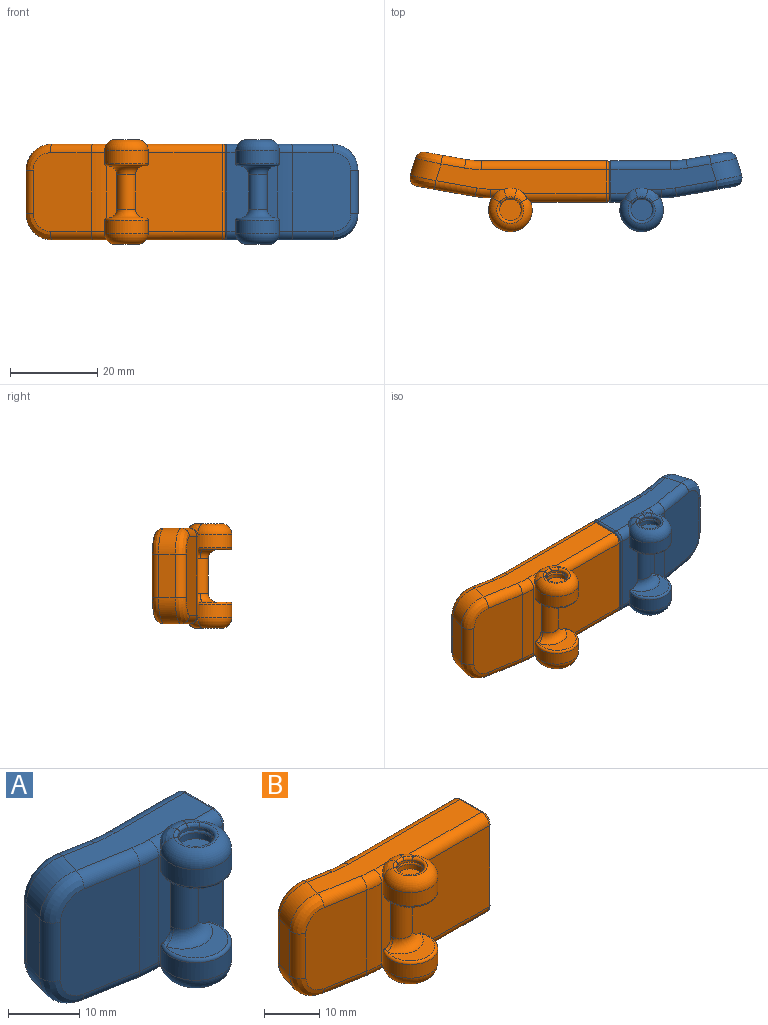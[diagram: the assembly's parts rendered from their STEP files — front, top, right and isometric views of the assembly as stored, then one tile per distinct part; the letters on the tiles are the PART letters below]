
ASSEMBLY  parts=2 mates=1
PART A: 91 faces, bbox 31x19.4x24.6 mm
  f0: plane 24.55x7.21mm, normal (0,0,-1), area 106.2mm2, adj f10,f23,f24,f25,f32,f33,f34,f42
  f1: plane 21x8.5mm, normal (1,0,0), area 116.5mm2, adj f18,f19,f20,f21,f67,f68,f69,f70
  f2: plane 10x3.86mm, normal (-0.96,0.28,0), area 40.3mm2, adj f7,f10,f27,f36
  f3: plane 9x6.24mm, normal (0,0,1), area 26.5mm2, adj f43,f78
  f4: cylinder r=2.25mm len=8.16mm, axis (0,0,1), area 50mm2, adj f13,f17,f77,f78,f80,f81
  f5: plane 9x6.24mm, normal (0,0,-1), area 26.5mm2, adj f44,f81
  f6: cylinder r=5mm len=10mm, axis (0,0,1), area 61.4mm2, adj f13,f17,f40,f41,f44,f60
  f7: cylinder r=6mm len=7.02mm, axis (0.28,0.96,0), area 37.9mm2, adj f2,f15,f28,f37
  f8: cylinder r=20mm len=18mm, axis (0,0,1), area 62.8mm2, adj f9,f16,f24,f30
  f9: plane 18x9.36mm, normal (0.17,0.98,0), area 164.2mm2, adj f8,f25,f26,f27,f28,f29
  f10: cylinder r=6mm len=7.02mm, axis (-0.28,-0.96,0), area 37.9mm2, adj f0,f2,f26,f35
  f11: plane 18x13.34mm, normal (-0.17,-0.98,0), area 236.8mm2, adj f12,f34,f35,f36,f37,f38
  f12: cylinder r=20mm len=18mm, axis (0,0,-1), area 62.8mm2, adj f11,f13,f33,f39
  f13: plane 18.17x2.48mm, normal (0,-1,0), area 28.9mm2, adj f4,f6,f12,f14,f32,f40,f43,f44
  f14: cylinder r=5mm len=10mm, axis (0,0,-1), area 61.4mm2, adj f13,f17,f32,f42,f43,f56
  f15: plane 24.55x7.21mm, normal (0,0,1), area 106.2mm2, adj f7,f29,f30,f31,f38,f39,f40,f41
  f16: plane 18x13.77mm, normal (0,1,0), area 222.6mm2, adj f8,f23,f31,f67,f75,f76
  f17: plane 18.11x5.11mm, normal (0,-1,0), area 72.7mm2, adj f4,f6,f14,f41,f42,f43,f44,f74
  f18: plane 20x4.9mm, normal (0,0,-1), area 98mm2, adj f1,f19,f21,f22
  f19: plane 20x12.25mm, normal (0,1,0), area 245mm2, adj f1,f18,f20,f22
  f20: plane 20x4.9mm, normal (0,0,1), area 98mm2, adj f1,f19,f21,f22
  f21: plane 20x12.25mm, normal (0,-1,0), area 245mm2, adj f1,f18,f20,f22
  f22: plane 12.25x4.9mm, normal (1,0,0), area 60mm2, adj f18,f19,f20,f21
  f23: cylinder r=2mm len=13.77mm, axis (-1,0,0), area 43.2mm2, adj f0,f16,f24,f69
  f24: torus R=22mm, axis (0,0,1), area 11.4mm2, adj f0,f8,f23,f25
  f25: cylinder r=2mm len=5.75mm, axis (-0.98,0.17,0), area 17.2mm2, adj f0,f9,f24,f26
  f26: bspline ~7.26x6.01mm, area 24.7mm2, adj f9,f10,f25,f27
  f27: cylinder r=2mm len=10mm, axis (0,0,-1), area 29.2mm2, adj f2,f9,f26,f28
  f28: bspline ~7.26x7.05mm, area 24.7mm2, adj f7,f9,f27,f29
  f29: cylinder r=2mm len=5.75mm, axis (0.98,-0.17,0), area 17.2mm2, adj f9,f15,f28,f30
  f30: torus R=22mm, axis (0,0,1), area 11.4mm2, adj f8,f15,f29,f31
  f31: cylinder r=2mm len=13.77mm, axis (1,0,0), area 43.2mm2, adj f15,f16,f30,f68
  f32: cylinder r=2mm len=3.06mm, axis (-1,0,0), area 3.5mm2, adj f0,f13,f14,f33,f58
  f33: torus R=18mm, axis (0,0,1), area 10.6mm2, adj f0,f12,f32,f34
  f34: cylinder r=2mm len=9.72mm, axis (0.98,-0.17,0), area 29.9mm2, adj f0,f11,f33,f35
  f35: bspline ~6x5.96mm, area 27.4mm2, adj f10,f11,f34,f36
  f36: cylinder r=2mm len=10mm, axis (0,0,1), area 33.7mm2, adj f2,f11,f35,f37
  f37: bspline ~6x5.96mm, area 27.4mm2, adj f7,f11,f36,f38
  f38: cylinder r=2mm len=9.72mm, axis (-0.98,0.17,0), area 29.9mm2, adj f11,f15,f37,f39
  f39: torus R=18mm, axis (0,0,1), area 10.6mm2, adj f12,f15,f38,f40
  f40: cylinder r=2mm len=3.06mm, axis (1,0,0), area 3.5mm2, adj f6,f13,f15,f39,f59
  f41: cylinder r=2mm len=4mm, axis (-1,0,0), area 9.5mm2, adj f6,f15,f17,f60,f62,f72
  f42: cylinder r=2mm len=4mm, axis (1,0,0), area 9.5mm2, adj f0,f14,f17,f55,f56,f73
  f43: torus R=4.5mm, axis (0,0,-1), area 15.5mm2, adj f3,f13,f14,f17,f77,f79
  f44: torus R=4.5mm, axis (0,0,-1), area 15.5mm2, adj f5,f6,f13,f17,f80,f82
  f45: plane 6x6mm, normal (0,0,-1), area 8.6mm2, adj f46,f49
  f46: cylinder r=2.5mm len=5mm, axis (0,0,-1), area 7.1mm2, adj f45,f83,f84,f85,f86
  f47: plane 5x5mm, normal (0,0,1), area 19.6mm2, adj f48
  f48: cylinder r=2.5mm len=5mm, axis (0,0,1), area 15.7mm2, adj f47,f49
  f49: torus R=3mm, axis (0,0,1), area 13.2mm2, adj f45,f48
  f50: plane 6x6mm, normal (0,0,1), area 8.6mm2, adj f51,f54
  f51: cylinder r=2.5mm len=5mm, axis (0,0,1), area 7.1mm2, adj f50,f87,f88,f89,f90
  f52: plane 5x5mm, normal (0,0,-1), area 19.6mm2, adj f53
  f53: cylinder r=2.5mm len=5mm, axis (0,0,-1), area 15.7mm2, adj f52,f54
  f54: torus R=3mm, axis (0,0,1), area 13.2mm2, adj f50,f53
  f55: bspline ~3.66x3.42mm, area 5.7mm2, adj f0,f42,f56,f57,f90
  f56: torus R=2.5mm, axis (0,0,-1), area 61.4mm2, adj f14,f42,f55,f58,f89
  f57: torus R=3mm, axis (0,0,1), area 5.8mm2, adj f0,f55,f58,f88
  f58: bspline ~3.54x3.33mm, area 6.8mm2, adj f32,f56,f57,f87
  f59: bspline ~3.66x3.42mm, area 6.8mm2, adj f40,f60,f61,f86
  f60: torus R=2.5mm, axis (0,0,1), area 61.4mm2, adj f6,f41,f59,f62,f85
  f61: torus R=3mm, axis (0,0,-1), area 5.8mm2, adj f15,f59,f62,f84
  f62: bspline ~3.54x3.33mm, area 5.7mm2, adj f15,f41,f60,f61,f83
  f63: cylinder r=1.5mm len=3mm, axis (0,1,0), area 4.7mm2, adj f64,f75
  f64: plane 3x3mm, normal (0,1,0), area 7.1mm2, adj f63
  f65: cylinder r=1.5mm len=3mm, axis (0,1,0), area 4.7mm2, adj f66,f76
  f66: plane 3x3mm, normal (0,1,0), area 7.1mm2, adj f65
  f67: cylinder r=0.5mm len=18mm, axis (0,0,-1), area 14.1mm2, adj f1,f16,f68,f69
  f68: torus R=1.5mm, axis (1,0,0), area 2.2mm2, adj f1,f31,f67,f70
  f69: torus R=1.5mm, axis (1,0,0), area 2.2mm2, adj f1,f23,f67,f71
  f70: cylinder r=0.5mm len=5.5mm, axis (0,1,0), area 4.3mm2, adj f1,f15,f68,f72
  f71: cylinder r=0.5mm len=5.5mm, axis (0,-1,0), area 4.3mm2, adj f0,f1,f69,f73
  f72: torus R=1.5mm, axis (1,0,0), area 2.2mm2, adj f1,f41,f70,f74
  f73: torus R=1.5mm, axis (1,0,0), area 2.2mm2, adj f1,f42,f71,f74
  f74: cylinder r=0.5mm len=18mm, axis (0,0,1), area 14.1mm2, adj f1,f17,f72,f73
  f75: torus R=2mm, axis (0,1,0), area 8.3mm2, adj f16,f63
  f76: torus R=2mm, axis (0,1,0), area 8.3mm2, adj f16,f65
  f77: bspline ~2.32x2.19mm, area 2mm2, adj f4,f13,f43,f78
  f78: torus R=4.25mm, axis (0,0,-1), area 24.5mm2, adj f3,f4,f17,f77,f79
  f79: bspline ~2.32x2.19mm, area 0mm2, adj f17,f43,f78
  f80: bspline ~2.32x2.19mm, area 2mm2, adj f4,f13,f44,f81
  f81: torus R=4.25mm, axis (0,0,-1), area 24.5mm2, adj f4,f5,f17,f80,f82
  f82: bspline ~2.32x2.19mm, area 0mm2, adj f17,f44,f81
  f83: bspline ~2.15x1.64mm, area 1.5mm2, adj f46,f62,f84,f85
  f84: torus R=3mm, axis (0,0,1), area 1.3mm2, adj f46,f61,f83,f86
  f85: torus R=3mm, axis (0,0,-1), area 10.8mm2, adj f46,f60,f83,f86
  f86: bspline ~2.4x1.61mm, area 1.5mm2, adj f46,f59,f84,f85
  f87: bspline ~2.15x1.64mm, area 1.5mm2, adj f51,f58,f88,f89
  f88: torus R=3mm, axis (0,0,-1), area 1.3mm2, adj f51,f57,f87,f90
  f89: torus R=3mm, axis (0,0,1), area 10.8mm2, adj f51,f56,f87,f90
  f90: bspline ~2.4x1.61mm, area 1.5mm2, adj f51,f55,f88,f89
PART B: 91 faces, bbox 46x19.4x24.6 mm
  f0: plane 39.55x7.21mm, normal (0,0,-1), area 188.7mm2, adj f10,f23,f24,f25,f32,f33,f34,f42
  f1: plane 21x8.5mm, normal (1,0,0), area 105.5mm2, adj f18,f19,f20,f21,f67,f68,f69,f70
  f2: plane 10x3.86mm, normal (-0.96,0.28,0), area 40.3mm2, adj f7,f10,f27,f36
  f3: plane 9x6.24mm, normal (0,0,1), area 26.5mm2, adj f43,f78
  f4: cylinder r=2.25mm len=8.16mm, axis (0,0,1), area 50mm2, adj f13,f17,f77,f78,f80,f81
  f5: plane 9x6.24mm, normal (0,0,-1), area 26.5mm2, adj f44,f81
  f6: cylinder r=5mm len=10mm, axis (0,0,1), area 61.4mm2, adj f13,f17,f40,f41,f44,f60
  f7: cylinder r=6mm len=7.02mm, axis (0.28,0.96,0), area 37.9mm2, adj f2,f15,f28,f37
  f8: cylinder r=20mm len=18mm, axis (0,0,1), area 62.8mm2, adj f9,f16,f24,f30
  f9: plane 18x9.36mm, normal (0.17,0.98,0), area 164.2mm2, adj f8,f25,f26,f27,f28,f29
  f10: cylinder r=6mm len=7.02mm, axis (-0.28,-0.96,0), area 37.9mm2, adj f0,f2,f26,f35
  f11: plane 18x13.34mm, normal (-0.17,-0.98,0), area 236.8mm2, adj f12,f34,f35,f36,f37,f38
  f12: cylinder r=20mm len=18mm, axis (0,0,-1), area 62.8mm2, adj f11,f13,f33,f39
  f13: plane 18.17x2.48mm, normal (0,-1,0), area 28.9mm2, adj f4,f6,f12,f14,f32,f40,f43,f44
  f14: cylinder r=5mm len=10mm, axis (0,0,-1), area 61.4mm2, adj f13,f17,f32,f42,f43,f56
  f15: plane 39.55x7.21mm, normal (0,0,1), area 188.7mm2, adj f7,f29,f30,f31,f38,f39,f40,f41
  f16: plane 28.77x18mm, normal (0,1,0), area 492.6mm2, adj f8,f23,f31,f67,f75,f76
  f17: plane 20.11x18.11mm, normal (0,-1,0), area 342.7mm2, adj f4,f6,f14,f41,f42,f43,f44,f74
  f18: plane 35x4.9mm, normal (0,0,-1), area 171.5mm2, adj f1,f19,f21,f22
  f19: plane 35x14.5mm, normal (0,1,0), area 507.5mm2, adj f1,f18,f20,f22
  f20: plane 35x4.9mm, normal (0,0,1), area 171.5mm2, adj f1,f19,f21,f22
  f21: plane 35x14.5mm, normal (0,-1,0), area 507.5mm2, adj f1,f18,f20,f22
  f22: plane 14.5x4.9mm, normal (1,0,0), area 71mm2, adj f18,f19,f20,f21
  f23: cylinder r=2mm len=28.77mm, axis (-1,0,0), area 90.4mm2, adj f0,f16,f24,f69
  f24: torus R=22mm, axis (0,0,1), area 11.4mm2, adj f0,f8,f23,f25
  f25: cylinder r=2mm len=5.75mm, axis (-0.98,0.17,0), area 17.2mm2, adj f0,f9,f24,f26
  f26: bspline ~7.26x6.01mm, area 24.7mm2, adj f9,f10,f25,f27
  f27: cylinder r=2mm len=10mm, axis (0,0,-1), area 29.2mm2, adj f2,f9,f26,f28
  f28: bspline ~7.26x7.05mm, area 24.7mm2, adj f7,f9,f27,f29
  f29: cylinder r=2mm len=5.75mm, axis (0.98,-0.17,0), area 17.2mm2, adj f9,f15,f28,f30
  f30: torus R=22mm, axis (0,0,1), area 11.4mm2, adj f8,f15,f29,f31
  f31: cylinder r=2mm len=28.77mm, axis (1,0,0), area 90.4mm2, adj f15,f16,f30,f68
  f32: cylinder r=2mm len=3.06mm, axis (-1,0,0), area 3.5mm2, adj f0,f13,f14,f33,f58
  f33: torus R=18mm, axis (0,0,1), area 10.6mm2, adj f0,f12,f32,f34
  f34: cylinder r=2mm len=9.72mm, axis (0.98,-0.17,0), area 29.9mm2, adj f0,f11,f33,f35
  f35: bspline ~6x5.96mm, area 27.4mm2, adj f10,f11,f34,f36
  f36: cylinder r=2mm len=10mm, axis (0,0,1), area 33.7mm2, adj f2,f11,f35,f37
  f37: bspline ~6x5.96mm, area 27.4mm2, adj f7,f11,f36,f38
  f38: cylinder r=2mm len=9.72mm, axis (-0.98,0.17,0), area 29.9mm2, adj f11,f15,f37,f39
  f39: torus R=18mm, axis (0,0,1), area 10.6mm2, adj f12,f15,f38,f40
  f40: cylinder r=2mm len=3.06mm, axis (1,0,0), area 3.5mm2, adj f6,f13,f15,f39,f59
  f41: cylinder r=2mm len=19mm, axis (-1,0,0), area 56.6mm2, adj f6,f15,f17,f60,f62,f72
  f42: cylinder r=2mm len=19mm, axis (1,0,0), area 56.6mm2, adj f0,f14,f17,f55,f56,f73
  f43: torus R=4.5mm, axis (0,0,-1), area 15.5mm2, adj f3,f13,f14,f17,f77,f79
  f44: torus R=4.5mm, axis (0,0,-1), area 15.5mm2, adj f5,f6,f13,f17,f80,f82
  f45: plane 6x6mm, normal (0,0,-1), area 8.6mm2, adj f46,f49
  f46: cylinder r=2.5mm len=5mm, axis (0,0,-1), area 7.1mm2, adj f45,f83,f84,f85,f86
  f47: plane 5x5mm, normal (0,0,1), area 19.6mm2, adj f48
  f48: cylinder r=2.5mm len=5mm, axis (0,0,1), area 15.7mm2, adj f47,f49
  f49: torus R=3mm, axis (0,0,1), area 13.2mm2, adj f45,f48
  f50: plane 6x6mm, normal (0,0,1), area 8.6mm2, adj f51,f54
  f51: cylinder r=2.5mm len=5mm, axis (0,0,1), area 7.1mm2, adj f50,f87,f88,f89,f90
  f52: plane 5x5mm, normal (0,0,-1), area 19.6mm2, adj f53
  f53: cylinder r=2.5mm len=5mm, axis (0,0,-1), area 15.7mm2, adj f52,f54
  f54: torus R=3mm, axis (0,0,1), area 13.2mm2, adj f50,f53
  f55: bspline ~3.66x3.42mm, area 5.7mm2, adj f0,f42,f56,f57,f90
  f56: torus R=2.5mm, axis (0,0,-1), area 61.4mm2, adj f14,f42,f55,f58,f89
  f57: torus R=3mm, axis (0,0,1), area 5.8mm2, adj f0,f55,f58,f88
  f58: bspline ~3.54x3.33mm, area 6.8mm2, adj f32,f56,f57,f87
  f59: bspline ~3.66x3.42mm, area 6.8mm2, adj f40,f60,f61,f86
  f60: torus R=2.5mm, axis (0,0,1), area 61.4mm2, adj f6,f41,f59,f62,f85
  f61: torus R=3mm, axis (0,0,-1), area 5.8mm2, adj f15,f59,f62,f84
  f62: bspline ~3.54x3.33mm, area 5.7mm2, adj f15,f41,f60,f61,f83
  f63: cylinder r=1.5mm len=3mm, axis (0,1,0), area 4.7mm2, adj f64,f75
  f64: plane 3x3mm, normal (0,1,0), area 7.1mm2, adj f63
  f65: cylinder r=1.5mm len=3mm, axis (0,1,0), area 4.7mm2, adj f66,f76
  f66: plane 3x3mm, normal (0,1,0), area 7.1mm2, adj f65
  f67: cylinder r=0.5mm len=18mm, axis (0,0,-1), area 14.1mm2, adj f1,f16,f68,f69
  f68: torus R=1.5mm, axis (1,0,0), area 2.2mm2, adj f1,f31,f67,f70
  f69: torus R=1.5mm, axis (1,0,0), area 2.2mm2, adj f1,f23,f67,f71
  f70: cylinder r=0.5mm len=5.5mm, axis (0,1,0), area 4.3mm2, adj f1,f15,f68,f72
  f71: cylinder r=0.5mm len=5.5mm, axis (0,-1,0), area 4.3mm2, adj f0,f1,f69,f73
  f72: torus R=1.5mm, axis (1,0,0), area 2.2mm2, adj f1,f41,f70,f74
  f73: torus R=1.5mm, axis (1,0,0), area 2.2mm2, adj f1,f42,f71,f74
  f74: cylinder r=0.5mm len=18mm, axis (0,0,1), area 14.1mm2, adj f1,f17,f72,f73
  f75: torus R=2mm, axis (0,1,0), area 8.3mm2, adj f16,f63
  f76: torus R=2mm, axis (0,1,0), area 8.3mm2, adj f16,f65
  f77: bspline ~2.32x2.19mm, area 2mm2, adj f4,f13,f43,f78
  f78: torus R=4.25mm, axis (0,0,-1), area 24.5mm2, adj f3,f4,f17,f77,f79
  f79: bspline ~2.32x2.19mm, area 0mm2, adj f17,f43,f78
  f80: bspline ~2.32x2.19mm, area 2mm2, adj f4,f13,f44,f81
  f81: torus R=4.25mm, axis (0,0,-1), area 24.5mm2, adj f4,f5,f17,f80,f82
  f82: bspline ~2.32x2.19mm, area 0mm2, adj f17,f44,f81
  f83: bspline ~2.15x1.64mm, area 1.5mm2, adj f46,f62,f84,f85
  f84: torus R=3mm, axis (0,0,1), area 1.3mm2, adj f46,f61,f83,f86
  f85: torus R=3mm, axis (0,0,-1), area 10.8mm2, adj f46,f60,f83,f86
  f86: bspline ~2.4x1.61mm, area 1.5mm2, adj f46,f59,f84,f85
  f87: bspline ~2.15x1.64mm, area 1.5mm2, adj f51,f58,f88,f89
  f88: torus R=3mm, axis (0,0,-1), area 1.3mm2, adj f51,f57,f87,f90
  f89: torus R=3mm, axis (0,0,1), area 10.8mm2, adj f51,f56,f87,f90
  f90: bspline ~2.4x1.61mm, area 1.5mm2, adj f51,f55,f88,f89
PLACE A rot(axis=(0,1,0),180deg) t=(59.7,13.99,-7.85)mm
PLACE B t=(22.7,13.99,-29.85)mm
MATE fastened A.f1 <-> B.f1  axis (-1,0,0) through (48.7,17.74,-18.85)mm
